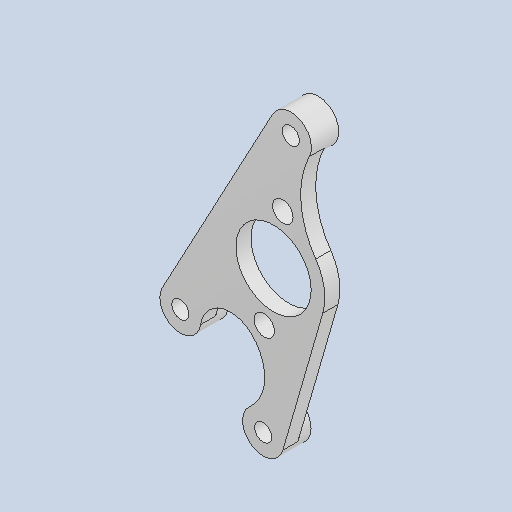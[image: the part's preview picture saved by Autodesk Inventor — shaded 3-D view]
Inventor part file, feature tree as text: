
AUTODESK INVENTOR PART (.ipt)
format: ipt  version: 2023 (Build 270158030, 158C)  size: 137,728 bytes
history: native  units: mm
features: other x3, sketch x1
ambient origin geometry x8: Origin, YZ Plane, XZ Plane, XY Plane, X Axis, Y Axis, Z Axis, Center Point
bodies: Solid2 (feature_tree)
feature tree (4):
  other  "モータマウント.ipt"
  other  "Solid2::モータマウント.ipt"
  other  "TaggingFeature1"
  sketch  "Sketch1"  dims[d0=10.0mm]
